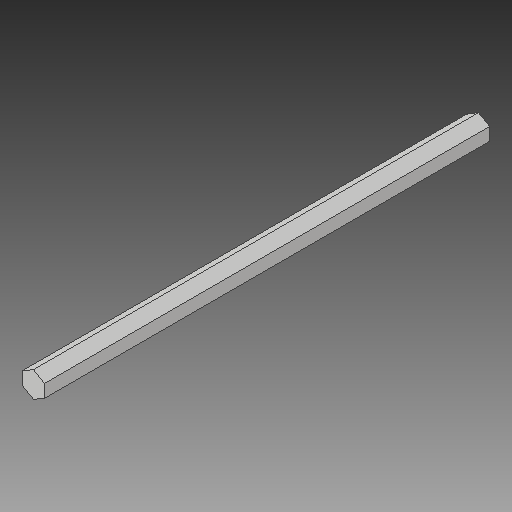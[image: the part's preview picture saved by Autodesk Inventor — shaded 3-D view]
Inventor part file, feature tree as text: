
AUTODESK INVENTOR PART (.ipt)
format: ipt  version: 2018 (Build 220112000, 112)  size: 96,256 bytes
history: native  units: in
note: dims shown in document units (in); Inventor stores cm internally (conversion verified against a paired STEP export)
features: extrude x1, sketch x1
ambient origin geometry x8: Origin, YZ Plane, XZ Plane, XY Plane, X Axis, Y Axis, Z Axis, Center Point
bodies: Solid1 (feature_tree)
feature tree (2):
  extrude  "Extrusion1"  Depth=10.0in TaperAngle=0.0deg
  sketch  "Sketch1"  dims[d0=0.25in d1=10.0in d2=0.0in]
